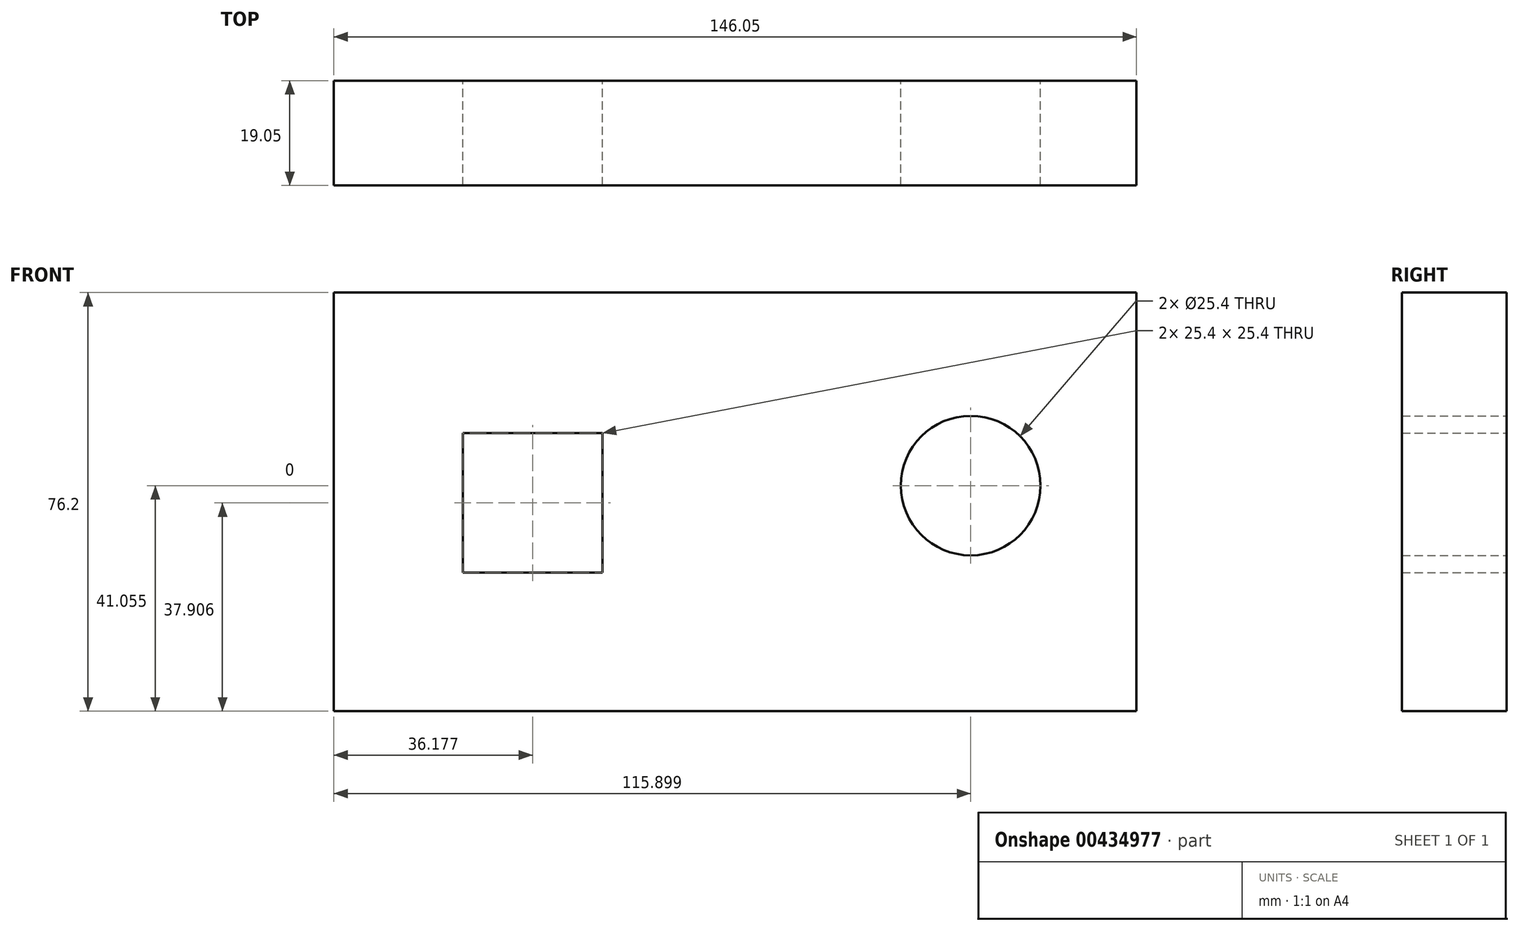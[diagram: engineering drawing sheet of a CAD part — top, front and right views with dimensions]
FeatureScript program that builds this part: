
annotation { "Feature Type Name" : "Feature", "Feature Type Description" : "" }
export const myFeature = defineFeature(function(context is Context, id is Id, definition is map)
    precondition{}
    {
        {
            var Q0;
            Q0=qCreatedBy(makeId("Front.planeOp"),FACE);
            var sketch = newSketch(context, id + "F0", { "sketchPlane" : qUnion([Q0])});
            skLineSegment(sketch, "E0", {"start": v(0, 0) * mm, "end": v(0, 76.2) * mm});
            skLineSegment(sketch, "E1", {"start": v(0, 76.2) * mm, "end": v(-146.05, 76.2) * mm});
            skLineSegment(sketch, "E2", {"start": v(-146.05, 76.2) * mm, "end": v(-146.05, 0) * mm});
            skLineSegment(sketch, "E3", {"start": v(-146.05, 0) * mm, "end": v(0, 0) * mm});
            skCircle(sketch, "E4", {"center": v(-30.15, 41.06) * mm, "radius": 12.7 * mm});
            skLineSegment(sketch, "E5", {"start": v(-97.17, 50.6) * mm, "end": v(-97.17, 25.2) * mm});
            skLineSegment(sketch, "E6", {"start": v(-97.17, 25.2) * mm, "end": v(-122.57, 25.2) * mm});
            skLineSegment(sketch, "E7", {"start": v(-122.57, 25.2) * mm, "end": v(-122.57, 50.6) * mm});
            skLineSegment(sketch, "E8", {"start": v(-122.57, 50.6) * mm, "end": v(-97.17, 50.6) * mm});
            skSolve(sketch);
        }
        {
            var Q0;
            Q0=makeQuery(id+"F0.imprint","IMPRINT",FACE,{"disambiguationData":[TD([[makeQuery(id+"F0.imprint","IMPRINT",EDGE,{"derivedFrom":sQuery(id+"F0.wireOp",EDGE,"E0")}),1.0]])]});
            extrude(context, id + "F1", {"entities" : qUnion([Q0]), "depth" : 19.05 * mm});
        }
    });
